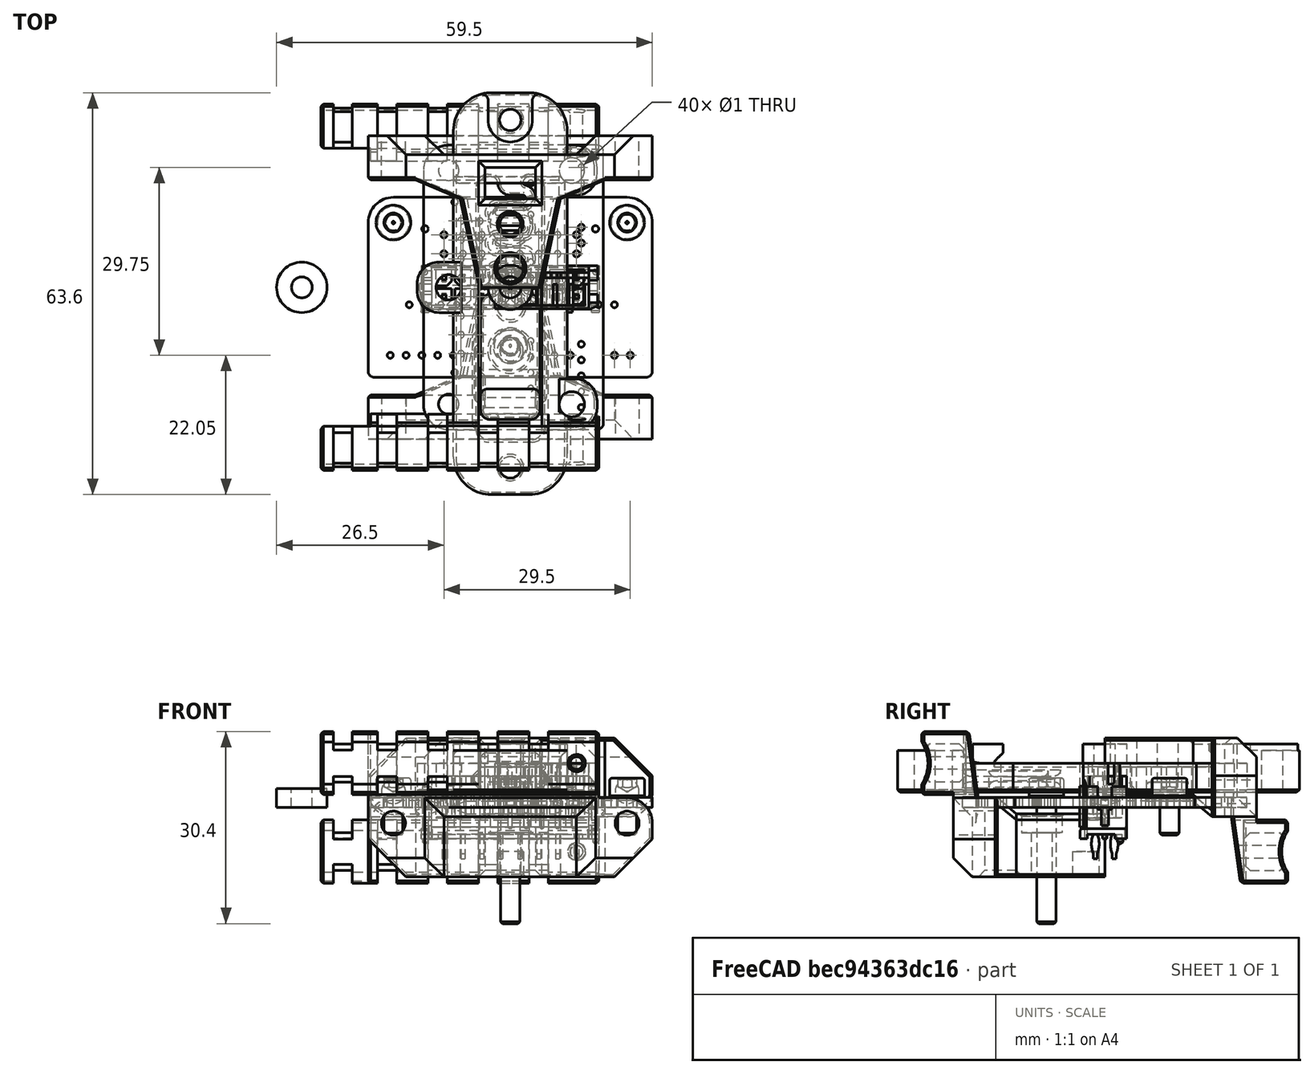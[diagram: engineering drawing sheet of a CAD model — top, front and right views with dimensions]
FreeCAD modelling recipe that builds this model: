
FCSTD DOCUMENT  (FreeCAD 0.19R24291 (Git))
Label: extruder-cable-guide-PCB
License: Other
LicenseURL: GPL3
objects: Part::Chamfer×20, Part::Feature×19, Part::Box×17, Part::MultiFuse×11, App::Part×10, Part::Cut×9, Part::Cylinder×7, Part::FeaturePython×4, Part::Fillet×2
note: 89 computed .brp shape members not serialized (recipe doc carries the construction recipe); baked Part::Feature solids carry a one-line shape summary decoded from their .brp

FEATURE [Part::Feature] Fusion001010
  Placement = pos=(-16,0,0) rot=(0,0,1;0rad)
  shape: bbox 3 x 9 x 10.5 mm, 12 faces, 2 solids (baked)
FEATURE [Part::Feature] Fusion001011
  Placement = pos=(-24,0,0) rot=(0,0,1;0rad)
  shape: bbox 3 x 9 x 10.5 mm, 12 faces, 2 solids (baked)
FEATURE [Part::Feature] Fusion001012
  Placement = pos=(-8,0,0) rot=(0,0,1;0rad)
  shape: bbox 3 x 9 x 10.5 mm, 12 faces, 2 solids (baked)
FEATURE [Part::Box] Box017  label="Cube017"
  AttacherType = Attacher::AttachEngine3D
  Height = 29
  Length = 8
  Placement = pos=(-4,14,-16) rot=(0,0,1;0rad)
  Width = 5
FEATURE [Part::Cylinder] Cylinder004
  Angle = 360
  AttacherType = Attacher::AttachEngine3D
  Height = 23
  Placement = pos=(10.5,13,-7) rot=(-1,0,0;1.5708rad)
  Radius = 1
FEATURE [Part::Box] Box020  label="Cube020"
  AttacherType = Attacher::AttachEngine3D
  Height = 2.5
  Length = 3
  Placement = pos=(3,22,-12.5) rot=(0,0,1;0rad)
  Width = 9
FEATURE [Part::Box] Box021  label="Cube021"
  AttacherType = Attacher::AttachEngine3D
  Height = 14
  Length = 27
  Placement = pos=(-13.5,26,-3) rot=(0,0,1;0rad)
  Width = 7
FEATURE [Part::Cylinder] Cylinder005
  Angle = 360
  AttacherType = Attacher::AttachEngine3D
  Height = 10
  Placement = pos=(18.5,29,5.5) rot=(-1,0,0;1.5708rad)
  Radius = 1.9
FEATURE [Part::Feature] Fusion001016
  Placement = pos=(-31,0,0) rot=(0,0,1;0rad)
  shape: bbox 3 x 9 x 10.5 mm, 12 faces, 2 solids (baked)
FEATURE [Part::Feature] Cut002003002014
  shape: bbox 15.84 x 14 x 11 mm, 11 faces (baked)
FEATURE [Part::Cylinder] Cylinder006
  Angle = 360
  AttacherType = Attacher::AttachEngine3D
  Height = 55
  Placement = pos=(19.5,34,-7) rot=(0.57735,0.57735,-0.57735;4.18879rad)
  Radius = 6
FEATURE [Part::Box] Box023  label="Cube023"
  AttacherType = Attacher::AttachEngine3D
  Height = 10
  Length = 58
  Placement = pos=(-33,26,8) rot=(0,0,1;0rad)
  Width = 10
FEATURE [Part::Chamfer] Chamfer001002006005039
  Base = -> Box023
  Edges = 1 edges r=3: [Edge9]
FEATURE [Part::Box] Box024  label="Cube024"
  AttacherType = Attacher::AttachEngine3D
  Height = 2
  Length = 3
  Placement = pos=(3,22,-4) rot=(0,0,1;0rad)
  Width = 9
FEATURE [Part::MultiFuse] Fusion001013
  Shapes = -> [Box024,Box020]
FEATURE [Part::MultiFuse] Fusion001014
  Shapes = -> [Fusion001016,Fusion001011,Fusion001010,Fusion001012,Fusion001013]
FEATURE [Part::Chamfer] Chamfer001002006005041
  Base = -> Box021
  Edges = 3 edges r=3: [Edge1,Edge5,Edge9]
  Placement = pos=(0,0,1.5) rot=(0,0,1;0rad)
FEATURE [Part::MultiFuse] Fusion001019
  Placement = pos=(0,-5,0) rot=(0,0,1;0rad)
  Shapes = -> [Chamfer001002006005041,Chamfer001002006005039]
FEATURE [Part::Cylinder] Cylinder007
  Angle = 360
  AttacherType = Attacher::AttachEngine3D
  Height = 10
  Placement = pos=(-18.5,29,5.5) rot=(-1,0,0;1.5708rad)
  Radius = 1.9
FEATURE [Part::MultiFuse] Fusion001017
  Placement = pos=(0,-14,-3) rot=(0,0,1;0rad)
  Shapes = -> [Cylinder007,Cylinder005]
FEATURE [Part::Box] Box026  label="Cube026"
  AttacherType = Attacher::AttachEngine3D
  Height = 12.5
  Length = 30
  Placement = pos=(-15,14,-1.5) rot=(0,0,1;0rad)
  Width = 4
FEATURE [Part::Feature] Part__Feature112001168  label="SOLID004"
  shape: bbox 12.4 x 5.75 x 10.4 mm, 141 faces (baked)
FEATURE [App::Part] JST_XH_B04B_XH_A_1x04_P2_50mm_Vertical  label="JST_XH_B04B-XH-A_1x04_P2.50mm_Vertical"
  Group = -> [Part__Feature112001168]
  Origin = -> Origin216
  Placement = pos=(-8.5,-2.75,1.65) rot=(0,0,1;3.14159rad)
FEATURE [Part::Feature] Part__Feature112001167  label="SOLID003"
  shape: bbox 9.9 x 5.75 x 10.4 mm, 117 faces (baked)
FEATURE [Part::FeaturePython] Screw003  label="M3x20-Screw025"  # Fasteners workbench fastener (typed FeaturePython)
  Placement = pos=(0,-9.25,1.6) rot=(0,0,1;0rad)
  baseObject = -> Part__Feature112001171 [Edge92]
  diameter = 4
  invert = false
  leftHanded = false
  length = 7
  lengthCustom = 20
  matchOuter = true
  offset = 0
  thread = false
  type = 34
FEATURE [Part::Feature] Part__Feature112001170  label="SOLID006"
  shape: bbox 2 x 1.25 x 1.25 mm, 28 faces (baked)
FEATURE [App::Part] C_0805_2012Metric
  Group = -> [Part__Feature112001170]
  Origin = -> Origin218
  Placement = pos=(-20.5,-3.225,1.65) rot=(0,0,1;1.5708rad)
FEATURE [Part::Feature] Part__Feature112001169  label="SOLID005"
  shape: bbox 14.9 x 5.75 x 10.4 mm, 165 faces (baked)
FEATURE [App::Part] JST_XH_B05B_XH_A_1x05_P2_50mm_Vertical  label="JST_XH_B05B-XH-A_1x05_P2.50mm_Vertical"
  Group = -> [Part__Feature112001169]
  Origin = -> Origin217
  Placement = pos=(-9,-10.75,1.65) rot=(0,0,1;3.14159rad)
FEATURE [App::Part] JST_XH_B03B_XH_A_1x03_P2_50mm_Vertical001  label="JST_XH_B03B-XH-A_1x03_P2.50mm_Vertical001"
  Group = -> [Part__Feature112001167]
  Origin = -> Origin215
  Placement = pos=(4,-2.75,1.65) rot=(0,0,1;3.14159rad)
FEATURE [Part::Feature] Part__Feature112001166  label="SOLID002"
  shape: bbox 7.4 x 5.75 x 10.4 mm, 89 faces (baked)
FEATURE [App::Part] JST_XH_B02B_XH_A_1x02_P2_50mm_Vertical001  label="JST_XH_B02B-XH-A_1x02_P2.50mm_Vertical001"
  Group = -> [Part__Feature112001166]
  Origin = -> Origin214
  Placement = pos=(9.5,-10.75,1.65) rot=(0,0,1;3.14159rad)
FEATURE [Part::Feature] Part__Feature112001171  label="COMPOUND002"
  shape: bbox 45 x 28.5 x 1.6 mm, 50 faces (baked)
FEATURE [Part::Feature] Part__Feature112001163  label="SOLID"
  shape: bbox 9.9 x 5.75 x 10.4 mm, 117 faces (baked)
FEATURE [Part::Feature] Part__Feature112001165  label="SOLID001"
  shape: bbox 7.4 x 5.75 x 10.4 mm, 89 faces (baked)
FEATURE [App::Part] JST_XH_B02B_XH_A_1x02_P2_50mm_Vertical  label="JST_XH_B02B-XH-A_1x02_P2.50mm_Vertical"
  Group = -> [Part__Feature112001165]
  Origin = -> Origin213
  Placement = pos=(19,-10.75,1.65) rot=(0,0,1;3.14159rad)
FEATURE [Part::Feature] Part__Feature112001164  label="COMPOUND"
  shape: bbox 28.15 x 8.8 x 13.09 mm, 388 faces (baked)
FEATURE [App::Part] COMPOUND  label="COMPOUND001"
  Group = -> [Part__Feature112001164]
  Origin = -> Origin211
FEATURE [App::Part] microfit_16  label="microfit-16"
  Group = -> [COMPOUND]
  Origin = -> Origin212
  Placement = pos=(-6e-06,6.81,6.65) rot=(0,0,1;0rad)
FEATURE [App::Part] JST_XH_B03B_XH_A_1x03_P2_50mm_Vertical  label="JST_XH_B03B-XH-A_1x03_P2.50mm_Vertical"
  Group = -> [Part__Feature112001163]
  Origin = -> Origin210
  Placement = pos=(16.5,-2.75,1.65) rot=(0,0,1;3.14159rad)
FEATURE [Part::FeaturePython] Screw001  label="M3x6-Screw001"  # Fasteners workbench fastener (typed FeaturePython)
  Placement = pos=(18.5,10.25,1.6) rot=(0,0,1;0rad)
  baseObject = -> Part__Feature112001171 [Edge78]
  diameter = 4
  invert = false
  leftHanded = false
  length = 1
  lengthCustom = 6
  matchOuter = true
  offset = 0
  thread = false
  type = 34
FEATURE [Part::FeaturePython] Screw002  label="M3x6-Screw"  # Fasteners workbench fastener (typed FeaturePython)
  Placement = pos=(-18.5,10.25,1.6) rot=(0,0,1;0rad)
  baseObject = -> Part__Feature112001171 [Edge81]
  diameter = 4
  invert = false
  leftHanded = false
  length = 1
  lengthCustom = 6
  matchOuter = true
  offset = 0
  thread = false
  type = 34
FEATURE [App::Part] Open_CASCADE_STEP_translator_6_9_1  label="PCB-rev1"
  Group = -> [JST_XH_B03B_XH_A_1x03_P2_50mm_Vertical,microfit_16,JST_XH_B02B_XH_A_1x02_P2_50mm_Vertical,JST_XH_B02B_XH_A_1x02_P2_50mm_Vertical001,JST_XH_B03B_XH_A_1x03_P2_50mm_Vertical001,JST_XH_B04B_XH_A_1x04_P2_50mm_Vertical,JST_XH_B05B_XH_A_1x05_P2_50mm_Vertical,C_0805_2012Metric,Part__Feature112001171,Screw002,Screw001,Screw003]
  Origin = -> Origin219
  Placement = pos=(0,24.05,12.75) rot=(1,0,0;4.71239rad)
FEATURE [Part::Box] Box027  label="Cube027"
  AttacherType = Attacher::AttachEngine3D
  Height = 10
  Length = 44
  Placement = pos=(-30,22,-12) rot=(0,0,1;0rad)
  Width = 7
FEATURE [Part::Box] Box028  label="Cube028"
  AttacherType = Attacher::AttachEngine3D
  Height = 12.5
  Length = 45
  Placement = pos=(-22.5,17,-1.5) rot=(0,0,1;0rad)
  Width = 7
FEATURE [Part::Fillet] Fillet002
  Base = -> Box028
  Edges = 2 edges r=4: [Edge4,Edge8]
FEATURE [Part::Chamfer] Chamfer001002006005046
  Base = -> Fillet002
  Edges = 2 edges r=6: [Edge4,Edge13]
FEATURE [Part::Chamfer] Chamfer001002006005047
  Base = -> Cut002003002014
  Edges = 4 edges r=0.4: [Edge7,Edge10,Edge14,Edge15]
FEATURE [Part::Chamfer] Chamfer001002006005049
  Base = -> Box026
  Edges = 1 edges: [Edge5 r1=3 r2=7.08]
FEATURE [Part::Feature] Fusion001014001
  Placement = pos=(0,-9,0) rot=(0,0,1;0rad)
  shape: bbox 34 x 9 x 10.5 mm, 60 faces, 10 solids (baked)
FEATURE [Part::MultiFuse] Fusion001014002
  Shapes = -> [Fusion001014001,Fusion001014]
FEATURE [Part::Box] Box029  label="Cube029"
  AttacherType = Attacher::AttachEngine3D
  Height = 15.5
  Length = 36.5
  Placement = pos=(-22.5,20,-12) rot=(0,0,1;0rad)
  Width = 4
FEATURE [Part::Cut] Cut002003002017
  Base = -> Box027
  Tool = -> Cylinder006
FEATURE [Part::Chamfer] Chamfer001002006005059
  Base = -> Cut002003002017
  Edges = 13 edges r=0.4: [Edge1,Edge2,Edge3,Edge4,Edge5,Edge6,Edge7,Edge8,Edge10,Edge12,Edge14,Edge15,Edge16]
FEATURE [Part::Box] Box030  label="Cube030"
  AttacherType = Attacher::AttachEngine3D
  Height = 10
  Length = 3
  Placement = pos=(-21,10.5,-13.5) rot=(0,0,1;0rad)
  Width = 10
FEATURE [Part::Box] Box031  label="Cube031"
  AttacherType = Attacher::AttachEngine3D
  Height = 10
  Length = 3
  Placement = pos=(-13,10.5,-13.5) rot=(0,0,1;0rad)
  Width = 10
FEATURE [Part::Box] Box032  label="Cube032"
  AttacherType = Attacher::AttachEngine3D
  Height = 10
  Length = 3
  Placement = pos=(-5,10.5,-13.5) rot=(0,0,1;0rad)
  Width = 10
FEATURE [Part::Box] Box033  label="Cube033"
  AttacherType = Attacher::AttachEngine3D
  Height = 10
  Length = 3
  Placement = pos=(3,10.5,-13.5) rot=(0,0,1;0rad)
  Width = 10
FEATURE [Part::MultiFuse] Fusion001014004
  Placement = pos=(0,1.5,0) rot=(0,0,1;0rad)
  Shapes = -> [Box033,Box030,Box031,Box032]
FEATURE [Part::Chamfer] Chamfer001002006005063
  Base = -> Chamfer001002006005046
  Edges = 8 edges r=0.4: [Edge1,Edge5,Edge6,Edge7,Edge8,Edge9,Edge10,Edge11]
FEATURE [Part::Box] Box034  label="Cube034"
  AttacherType = Attacher::AttachEngine3D
  Height = 1
  Length = 19
  Placement = pos=(-10,-3,0) rot=(0,0,1;0rad)
  Width = 22
FEATURE [Part::Cut] Cut002003002021
  Base = -> Chamfer001002006005047
  Tool = -> Box034
FEATURE [Part::Chamfer] Chamfer001002006005064
  Base = -> Cut002003002021
  Edges = 2 edges r=1: [Edge7,Edge9]
FEATURE [Part::Chamfer] Chamfer001002006005050
  Base = -> Chamfer001002006005049
  Edges = 1 edges: [Edge15 r1=7.08 r2=3]
FEATURE [Part::Chamfer] Chamfer001002006005051
  Base = -> Chamfer001002006005050
  Edges = 1 edges: [Edge14 r1=2.5 r2=3]
FEATURE [Part::Chamfer] Chamfer001002006005065
  Base = -> Chamfer001002006005051
  Edges = 1 edges: [Edge11 r1=0.17 r2=0.4]
FEATURE [Part::Chamfer] Chamfer001002006005066
  Base = -> Chamfer001002006005065
  Edges = 1 edges: [Edge10 r1=0.17 r2=0.4]
FEATURE [Part::Chamfer] Chamfer001002006005067
  Base = -> Chamfer001002006005066
  Edges = 1 edges: [Edge18 r1=0.95 r2=0.5]
FEATURE [Part::Chamfer] Chamfer001002006005068
  Base = -> Chamfer001002006005067
  Edges = 1 edges: [Edge17 r1=0.5 r2=0.95]
FEATURE [Part::Chamfer] Chamfer001002006005069
  Base = -> Chamfer001002006005064
  Edges = 1 edges r=0.4: [Edge12]
FEATURE [Part::Chamfer] Chamfer001002006005070
  Base = -> Box029
  Edges = 1 edges: [Edge9 r1=10.5 r2=1.5]
FEATURE [Part::Chamfer] Chamfer001002006005071
  Base = -> Chamfer001002006005070
  Edges = 6 edges r=0.4: [Edge1,Edge2,Edge3,Edge9,Edge10,Edge13]
FEATURE [Part::MultiFuse] Fusion001014005
  Shapes = -> [Chamfer001002006005059,Chamfer001002006005071]
FEATURE [Part::Cut] Cut002003002022
  Base = -> Fusion001014005
  Tool = -> Fusion001014002
FEATURE [Part::Cut] Cut002003002023
  Base = -> Cut002003002022
  Tool = -> Fusion001014004
FEATURE [Part::MultiFuse] Fusion001014006
  Shapes = -> [Chamfer001002006005069,Chamfer001002006005068,Chamfer001002006005063,Cut002003002023]
FEATURE [Part::Cut] Cut002003002024
  Base = -> Fusion001014006
  Tool = -> Fusion001019
FEATURE [Part::Cut] Cut002003002025
  Base = -> Cut002003002024
  Tool = -> Fusion001017
FEATURE [Part::Cut] Cut002003002026
  Base = -> Cut002003002025
  Refine = true
  Tool = -> Cylinder004
FEATURE [Part::Cut] Cut002003002027
  Base = -> Cut002003002026
  Tool = -> Box017
FEATURE [Part::Chamfer] Chamfer001002006005072
  Base = -> Cut002003002027
  Edges = 24 edges r=1: [Edge88,Edge89,Edge96,Edge97,Edge98,Edge99,Edge106,Edge107,Edge114,Edge115,Edge123,Edge125,Edge199,Edge201,Edge269,Edge270,Edge275,Edge276,Edge289,Edge291,Edge321,Edge322,Edge323,Edge324]
FEATURE [Part::Chamfer] Chamfer001002006005073
  Base = -> Chamfer001002006005072
  Edges = 2 edges r=0.4: [Edge89,Edge124]
FEATURE [Part::Feature] Chamfer001002006005073001
  Placement = pos=(0,0,0) rot=(1,0,0;3.14159rad)
  shape: bbox 52.5 x 29 x 23 mm, 192 faces (baked)
FEATURE [Part::Feature] Tube001
  shape: bbox 7 x 7 x 10 mm, 4 faces (baked)
FEATURE [Part::Feature] Part__Feature822001001  label="RS-25 PSU Bracket003"
  Placement = pos=(0,0,4.6) rot=(0,0,1;0rad)
  shape: bbox 18 x 63.6 x 7.6 mm, 163 faces (baked)
FEATURE [Part::Feature] Part__Feature822001002  label="COMPOUND003"
  Placement = pos=(0.5,-1e-16,0) rot=(0,0,1;1.5708rad)
  shape: bbox 28.5 x 45 x 1.6 mm, 50 faces (baked)
FEATURE [Part::Cylinder] Cylinder
  Angle = 360
  AttacherType = Attacher::AttachEngine3D
  Height = 10
  Placement = pos=(-9.75,18.5,0) rot=(0,0,1;0rad)
  Radius = 2
FEATURE [Part::Cylinder] Cylinder008
  Angle = 360
  AttacherType = Attacher::AttachEngine3D
  Height = 10
  Placement = pos=(-9.75,-18.5,0) rot=(0,0,1;0rad)
  Radius = 2
FEATURE [Part::Cylinder] Cylinder009
  Angle = 360
  AttacherType = Attacher::AttachEngine3D
  Height = 10
  Placement = pos=(9.75,0,0) rot=(0,0,1;0rad)
  Radius = 2
FEATURE [Part::MultiFuse] Fusion
  Placement = pos=(0,0,-3) rot=(0,0,1;0rad)
  Shapes = -> [Cylinder,Cylinder008,Cylinder009]
FEATURE [Part::Box] Box  label="Cube"
  AttacherType = Attacher::AttachEngine3D
  Height = 4.6
  Length = 6
  Placement = pos=(-13.75,14.5,0) rot=(0,0,1;0rad)
  Width = 8
FEATURE [Part::Box] Box035  label="Cube035"
  AttacherType = Attacher::AttachEngine3D
  Height = 4.6
  Length = 7
  Placement = pos=(7.75,-4,0) rot=(0,0,1;0rad)
  Width = 8
FEATURE [Part::Box] Box036  label="Cube036"
  AttacherType = Attacher::AttachEngine3D
  Height = 4.6
  Length = 6
  Placement = pos=(-13.75,-22.5,0) rot=(0,0,1;0rad)
  Width = 8
FEATURE [Part::MultiFuse] Fusion001014007
  Shapes = -> [Box,Box035,Box036]
FEATURE [Part::Fillet] Fillet
  Base = -> Fusion001014007
  Edges = 6 edges r=3.5: [Edge1,Edge3,Edge17,Edge19,Edge25,Edge27]
FEATURE [Part::Chamfer] Chamfer
  Base = -> Fillet
  Edges = 15 edges r=0.4: [Edge1,Edge5,Edge6,Edge8,Edge9,Edge19,Edge23,Edge25,Edge26,Edge27,Edge37,Edge41,Edge42,Edge44,Edge45]
FEATURE [Part::MultiFuse] Fusion001014008
  Shapes = -> [Chamfer,Part__Feature822001001]
FEATURE [Part::Cut] Cut
  Base = -> Fusion001014008
  Placement = pos=(-1e-15,0,7) rot=(0,1,0;3.14159rad)
  Refine = true
  Tool = -> Fusion
FEATURE [Part::FeaturePython] Tube  # WARN: FeaturePython — macro-defined, semantics opaque (R4)
  AttacherType = Attacher::AttachEngine3D
  Height = 3
  InnerRadius = 1.65
  OuterRadius = 4
  Placement = pos=(-33,0,0) rot=(0,0,1;0rad)
